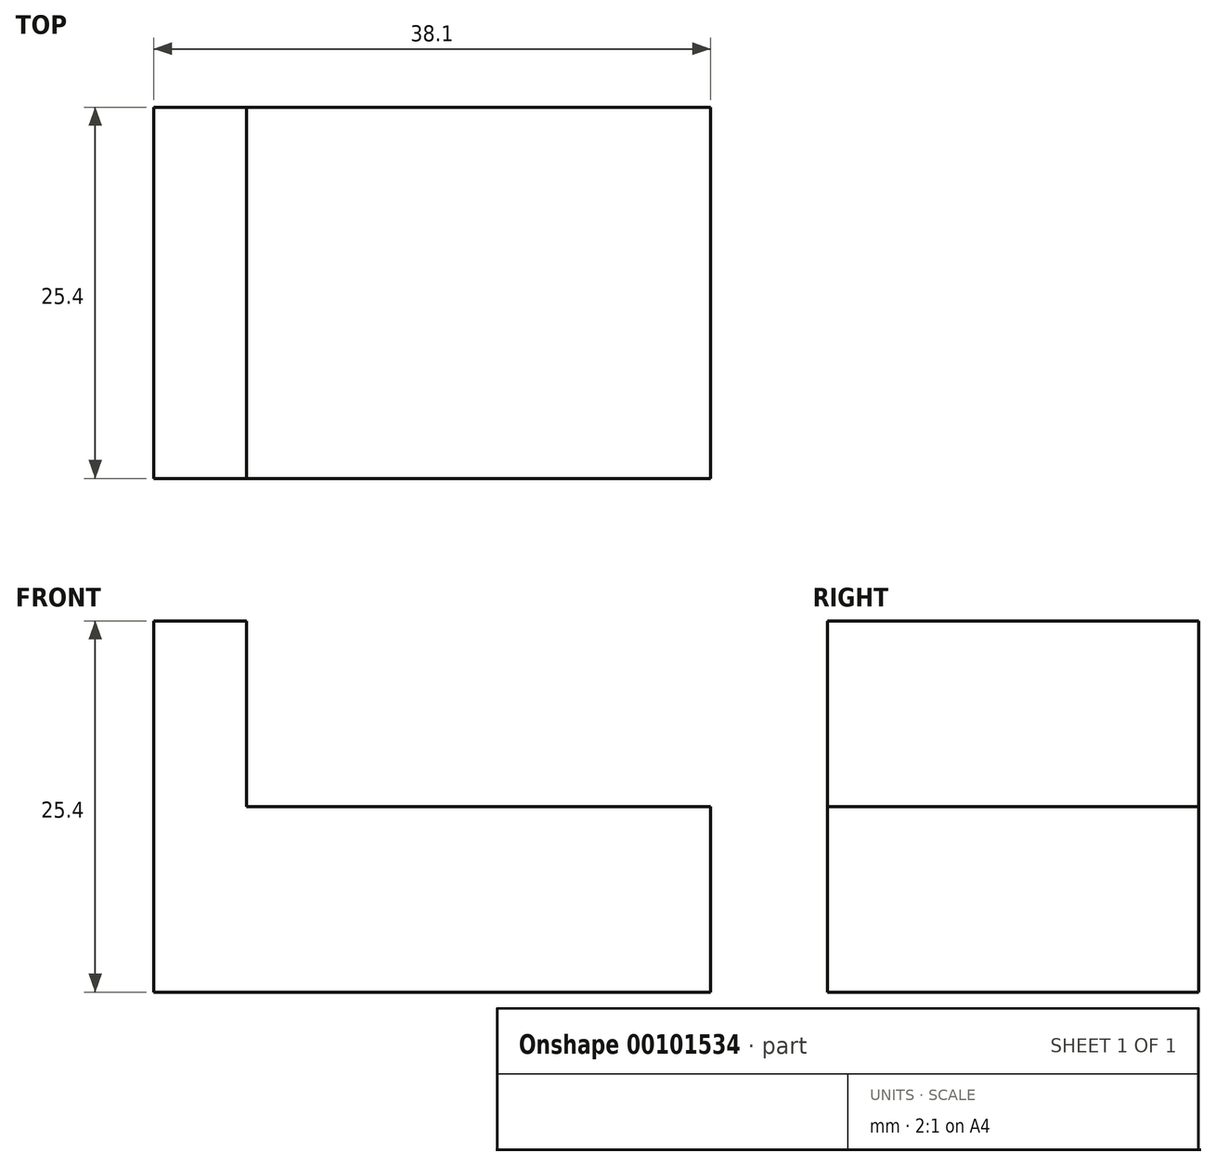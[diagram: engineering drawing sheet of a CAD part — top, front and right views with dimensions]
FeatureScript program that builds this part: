
annotation { "Feature Type Name" : "Feature", "Feature Type Description" : "" }
export const myFeature = defineFeature(function(context is Context, id is Id, definition is map)
    precondition{}
    {
        {
            var Q0;
            Q0=qCreatedBy(makeId("Front.planeOp"),FACE);
            var sketch = newSketch(context, id + "F0", { "sketchPlane" : qUnion([Q0])});
            skLineSegment(sketch, "E0", {"start": v(0, 0) * mm, "end": v(38.1, 0) * mm});
            skLineSegment(sketch, "E1", {"start": v(38.1, 0) * mm, "end": v(38.1, 12.7) * mm});
            skLineSegment(sketch, "E2", {"start": v(38.1, 12.7) * mm, "end": v(6.35, 12.7) * mm});
            skLineSegment(sketch, "E3", {"start": v(0, 0) * mm, "end": v(0, 25.4) * mm});
            skLineSegment(sketch, "E4", {"start": v(0, 25.4) * mm, "end": v(6.35, 25.4) * mm});
            skLineSegment(sketch, "E5", {"start": v(6.35, 25.4) * mm, "end": v(6.35, 12.7) * mm});
            skSolve(sketch);
        }
        {
            var Q0;
            Q0 = qSketchRegion(id + "F0", true);
            extrude(context, id + "F1", {"entities" : qUnion([Q0]), "depth" : 25.4 * mm});
        }
    });
